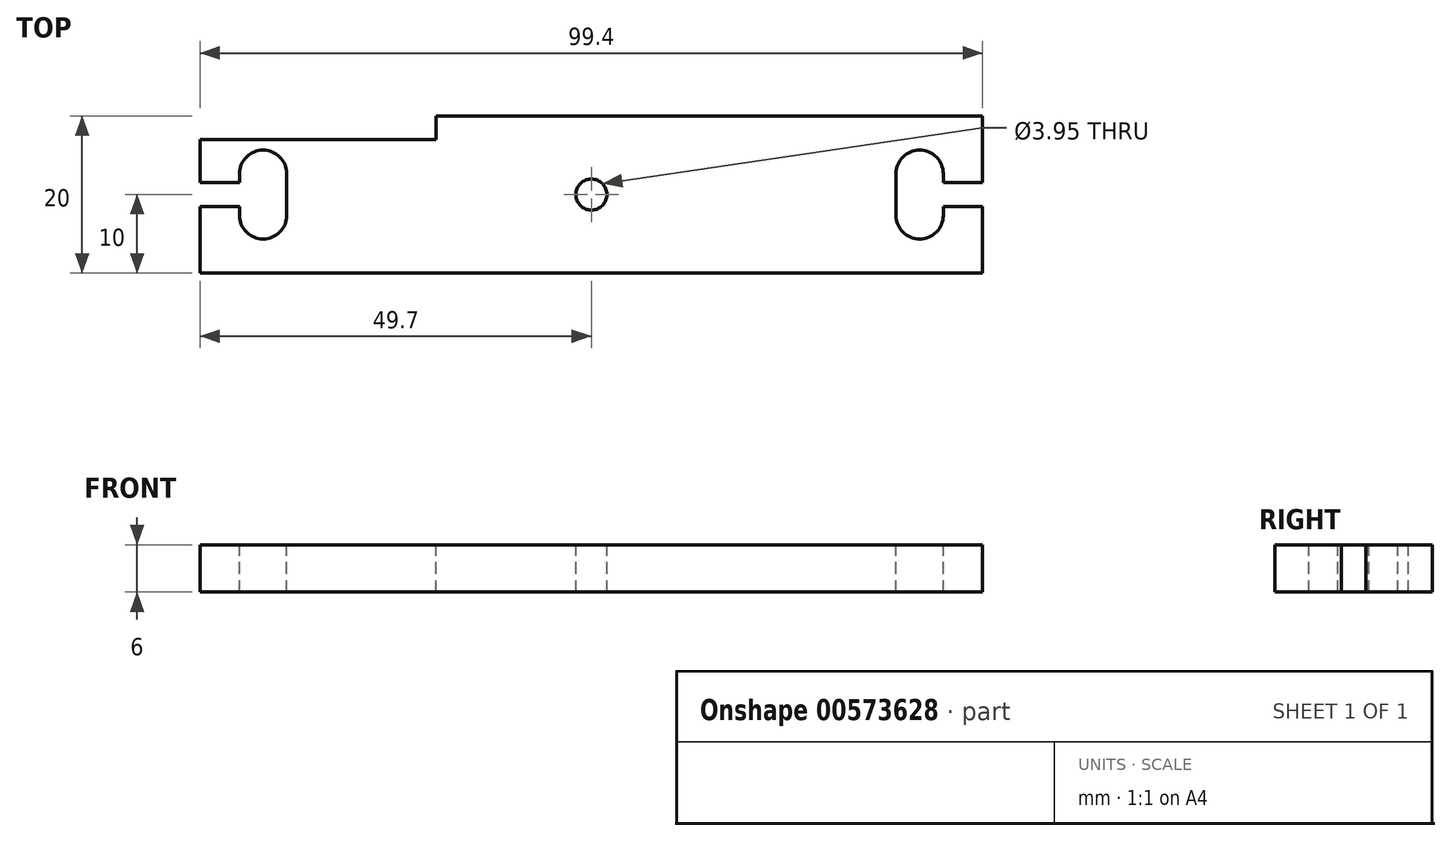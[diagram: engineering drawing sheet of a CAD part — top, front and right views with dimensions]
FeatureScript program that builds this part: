
annotation { "Feature Type Name" : "Feature", "Feature Type Description" : "" }
export const myFeature = defineFeature(function(context is Context, id is Id, definition is map)
    precondition{}
    {
        {
            var Q0;
            Q0=qCreatedBy(makeId("Top.planeOp"),FACE);
            var sketch = newSketch(context, id + "F0", { "sketchPlane" : qUnion([Q0])});
            skLineSegment(sketch, "E0.bottom", {"start": v(49.7, -10) * mm, "end": v(-49.7, -10) * mm});
            skLineSegment(sketch, "E0.top", {"start": v(49.7, 10) * mm, "end": v(-49.7, 10) * mm});
            skLineSegment(sketch, "E0.left", {"start": v(49.7, -10) * mm, "end": v(49.7, 10) * mm});
            skLineSegment(sketch, "E0.right", {"start": v(-49.7, -10) * mm, "end": v(-49.7, 10) * mm});
            skPoint(sketch, "E0.middle", {"position": v(0, 0) * mm});
            skSolve(sketch);
        }
        {
            var Q0;
            Q0=qSketchRegion(id+"F0",true);
            extrude(context, id + "F1", {"entities" : qUnion([Q0]), "depth" : 6 * mm, "offsetDistance" : 25 * mm});
        }
        {
            var Q0;
            Q0=makeQuery(id+"F1.opExtrude","CAP_FACE",FACE,{"disambiguationData":[OSD([sQuery(id+"F0.wireOp",EDGE,"E0.bottom"),sQuery(id+"F0.wireOp",EDGE,"E0.top"),sQuery(id+"F0.wireOp",EDGE,"E0.left"),sQuery(id+"F0.wireOp",EDGE,"E0.right")])],"isStart":false});
            var sketch = newSketch(context, id + "F2", { "sketchPlane" : qUnion([Q0])});
            skLineSegment(sketch, "E1", {"start": v(-49.7, 0) * mm, "end": v(49.7, 0) * mm, "construction": true});
            skLineSegment(sketch, "E2", {"start": v(0, 10) * mm, "end": v(0, -10) * mm, "construction": true});
            skLineSegment(sketch, "E3.bottom", {"start": v(-49.7, -1.55) * mm, "end": v(-38.7, -1.55) * mm});
            skLineSegment(sketch, "E3.top", {"start": v(-49.7, 1.55) * mm, "end": v(-38.7, 1.55) * mm});
            skLineSegment(sketch, "E3.left", {"start": v(-49.7, -1.55) * mm, "end": v(-49.7, 1.55) * mm});
            skLineSegment(sketch, "E3.right", {"start": v(-38.7, -1.55) * mm, "end": v(-38.7, 1.55) * mm});
            skLineSegment(sketch, "E4", {"start": v(-49.7, 0) * mm, "end": v(-38.7, 0) * mm, "construction": true});
            skLineSegment(sketch, "E5.right", {"start": v(-44.7, -2.65) * mm, "end": v(-44.7, 2.65) * mm});
            skPoint(sketch, "E5.middle", {"position": v(-43, 0) * mm});
            skArc(sketch, "E6", {"start": v(-38.7, 2.65) * mm, "mid": v(-41.7, 5.65) * mm, "end": v(-44.7, 2.65) * mm});
            skLineSegment(sketch, "E7", {"start": v(-38.7, 1.55) * mm, "end": v(-38.7, 2.65) * mm});
            skLineSegment(sketch, "E8", {"start": v(-38.7, 2.65) * mm, "end": v(-44.7, 2.65) * mm, "construction": true});
            skLineSegment(sketch, "E9", {"start": v(-38.7, -1.55) * mm, "end": v(-38.7, -2.65) * mm});
            skArc(sketch, "E10", {"start": v(-44.7, -2.65) * mm, "mid": v(-41.7, -5.65) * mm, "end": v(-38.7, -2.65) * mm});
            skPoint(sketch, "E11", {"position": v(-44.7, 0) * mm});
            skLineSegment(sketch, "E12.MirrorCS", {"start": v(38.7, 1.55) * mm, "end": v(38.7, 2.65) * mm});
            skLineSegment(sketch, "E13.MirrorCS", {"start": v(38.7, -1.55) * mm, "end": v(38.7, -2.65) * mm});
            skPoint(sketch, "E14.MirrorP", {"position": v(44.7, 0) * mm});
            skPoint(sketch, "E15.MirrorP", {"position": v(43, 0) * mm});
            skLineSegment(sketch, "E16.MirrorCS", {"start": v(38.7, -1.55) * mm, "end": v(38.7, 1.55) * mm});
            skLineSegment(sketch, "E17.MirrorCS", {"start": v(44.7, -2.65) * mm, "end": v(44.7, 2.65) * mm});
            skLineSegment(sketch, "E18.MirrorCS", {"start": v(49.7, -1.55) * mm, "end": v(49.7, 1.55) * mm});
            skLineSegment(sketch, "E19.MirrorCS", {"start": v(49.7, 1.55) * mm, "end": v(38.7, 1.55) * mm});
            skLineSegment(sketch, "E20.MirrorCS", {"start": v(49.7, -1.55) * mm, "end": v(38.7, -1.55) * mm});
            skLineSegment(sketch, "E21.MirrorCS", {"start": v(49.7, 0) * mm, "end": v(38.7, 0) * mm, "construction": true});
            skLineSegment(sketch, "E22.MirrorCS", {"start": v(38.7, 2.65) * mm, "end": v(44.7, 2.65) * mm, "construction": true});
            skArc(sketch, "E23.MirrorCS", {"start": v(38.7, 2.65) * mm, "mid": v(41.7, 5.65) * mm, "end": v(44.7, 2.65) * mm});
            skArc(sketch, "E24.MirrorCS", {"start": v(44.7, -2.65) * mm, "mid": v(41.7, -5.65) * mm, "end": v(38.7, -2.65) * mm});
            skSolve(sketch);
        }
        {
            var Q0;
            Q0=qSketchRegion(id+"F2",true);
            var Q1;
            Q1=makeQuery(id+"F1.opExtrude","CAP_FACE",FACE,{"disambiguationData":[OSD([sQuery(id+"F0.wireOp",EDGE,"E0.bottom"),sQuery(id+"F0.wireOp",EDGE,"E0.top"),sQuery(id+"F0.wireOp",EDGE,"E0.left"),sQuery(id+"F0.wireOp",EDGE,"E0.right")])],"isStart":true});
            extrude(context, id + "F3", {"entities" : qUnion([Q0]), "operationType" : NewBodyOperationType.REMOVE, "endBound" : BoundingType.UP_TO_SURFACE, "oppositeDirection" : true, "depth" : 25 * mm, "endBoundEntityFace" : qUnion([Q1]), "offsetDistance" : 25 * mm});
        }
        {
            var Q0;
            Q0=makeQuery(id+"F1.opExtrude","CAP_FACE",FACE,{"disambiguationData":[OSD([sQuery(id+"F0.wireOp",EDGE,"E0.bottom"),sQuery(id+"F0.wireOp",EDGE,"E0.top"),sQuery(id+"F0.wireOp",EDGE,"E0.left"),sQuery(id+"F0.wireOp",EDGE,"E0.right")])],"isStart":false});
            var sketch = newSketch(context, id + "F4", { "sketchPlane" : qUnion([Q0])});
            skCircle(sketch, "E25", {"center": v(0, 0) * mm, "radius": 1.98 * mm});
            skSolve(sketch);
        }
        {
            var Q0;
            Q0=qSketchRegion(id+"F4",true);
            var Q1;
            Q1=makeQuery(id+"F1.opExtrude","CAP_FACE",FACE,{"disambiguationData":[OSD([sQuery(id+"F0.wireOp",EDGE,"E0.bottom"),sQuery(id+"F0.wireOp",EDGE,"E0.top"),sQuery(id+"F0.wireOp",EDGE,"E0.left"),sQuery(id+"F0.wireOp",EDGE,"E0.right")])],"isStart":true});
            extrude(context, id + "F5", {"entities" : qUnion([Q0]), "operationType" : NewBodyOperationType.REMOVE, "endBound" : BoundingType.UP_TO_SURFACE, "oppositeDirection" : true, "depth" : 25 * mm, "endBoundEntityFace" : qUnion([Q1]), "offsetDistance" : 25 * mm});
        }
        {
            var Q0;
            Q0=makeQuery(id+"F1.opExtrude","CAP_FACE",FACE,{"disambiguationData":[OSD([sQuery(id+"F0.wireOp",EDGE,"E0.bottom"),sQuery(id+"F0.wireOp",EDGE,"E0.top"),sQuery(id+"F0.wireOp",EDGE,"E0.left"),sQuery(id+"F0.wireOp",EDGE,"E0.right")])],"isStart":false});
            var sketch = newSketch(context, id + "F6", { "sketchPlane" : qUnion([Q0])});
            skLineSegment(sketch, "E26.bottom", {"start": v(-49.7, 10) * mm, "end": v(-19.7, 10) * mm});
            skLineSegment(sketch, "E26.top", {"start": v(-49.7, 7) * mm, "end": v(-19.7, 7) * mm});
            skLineSegment(sketch, "E26.left", {"start": v(-49.7, 10) * mm, "end": v(-49.7, 7) * mm});
            skLineSegment(sketch, "E26.right", {"start": v(-19.7, 10) * mm, "end": v(-19.7, 7) * mm});
            skSolve(sketch);
        }
        {
            var Q0;
            Q0=qSketchRegion(id+"F6",true);
            var Q1;
            Q1=makeQuery(id+"F1.opExtrude","CAP_FACE",FACE,{"disambiguationData":[OSD([sQuery(id+"F0.wireOp",EDGE,"E0.bottom"),sQuery(id+"F0.wireOp",EDGE,"E0.top"),sQuery(id+"F0.wireOp",EDGE,"E0.left"),sQuery(id+"F0.wireOp",EDGE,"E0.right")])],"isStart":true});
            extrude(context, id + "F7", {"entities" : qUnion([Q0]), "operationType" : NewBodyOperationType.REMOVE, "endBound" : BoundingType.UP_TO_SURFACE, "oppositeDirection" : true, "depth" : 25 * mm, "endBoundEntityFace" : qUnion([Q1]), "offsetDistance" : 25 * mm});
        }
    });
